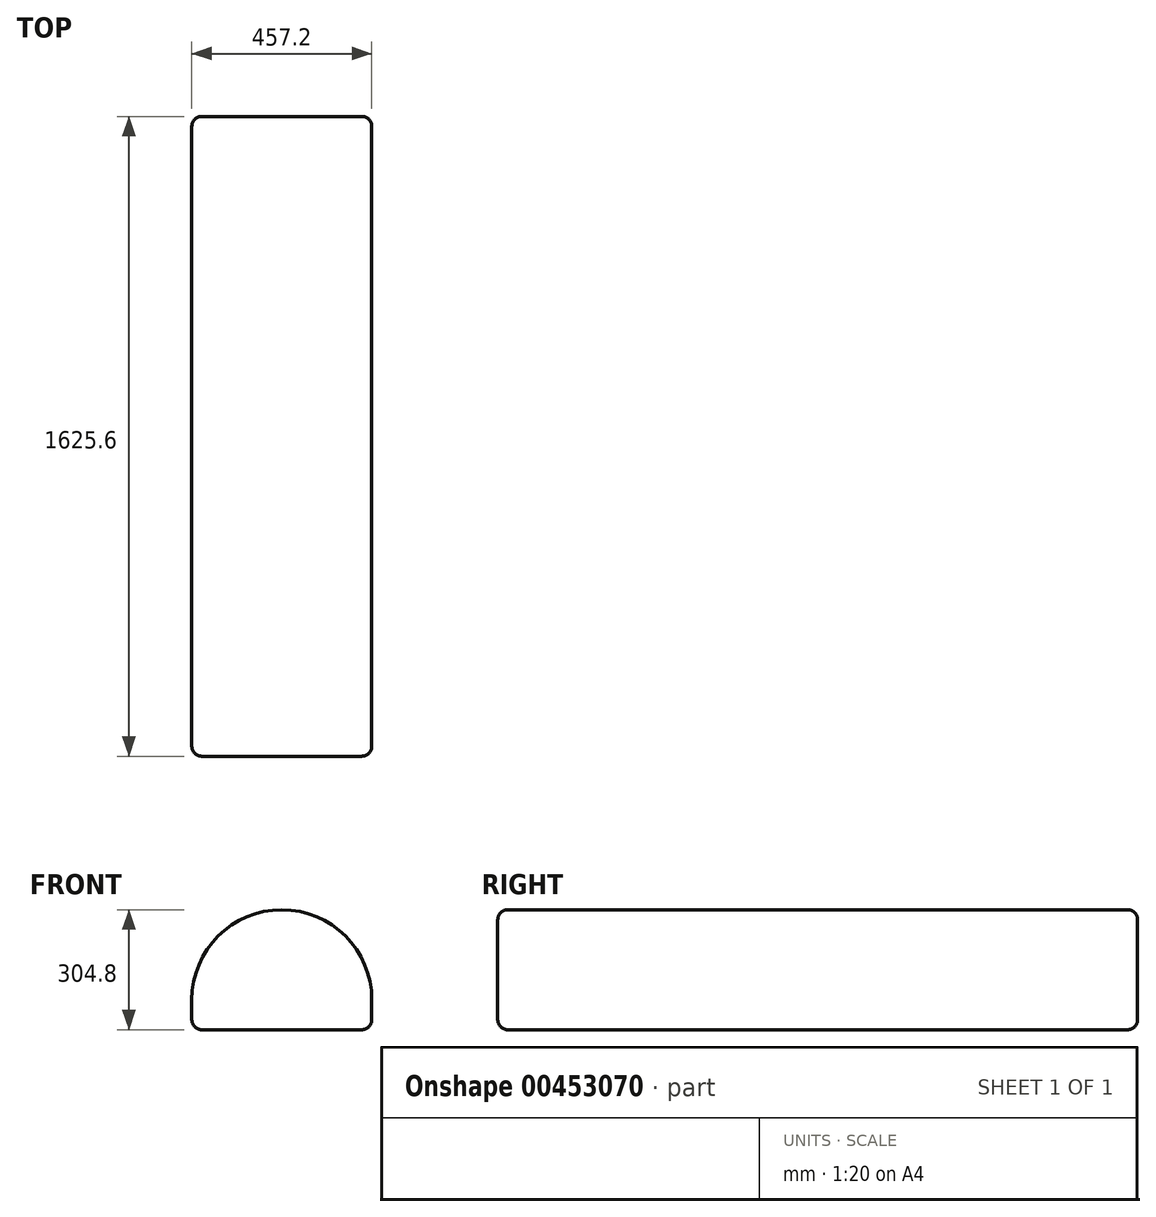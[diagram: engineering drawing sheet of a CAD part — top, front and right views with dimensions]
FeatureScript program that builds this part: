
annotation { "Feature Type Name" : "Feature", "Feature Type Description" : "" }
export const myFeature = defineFeature(function(context is Context, id is Id, definition is map)
    precondition{}
    {
        {
            var Q0;
            Q0=qCreatedBy(makeId("Front.planeOp"),FACE);
            var sketch = newSketch(context, id + "F0", { "sketchPlane" : qUnion([Q0])});
            skLineSegment(sketch, "E0", {"start": v(-228.6, 76.2) * mm, "end": v(-228.6, 0) * mm});
            skLineSegment(sketch, "E1", {"start": v(-228.6, 0) * mm, "end": v(228.6, 0) * mm});
            skLineSegment(sketch, "E2", {"start": v(228.6, 0) * mm, "end": v(228.6, 76.2) * mm});
            skArc(sketch, "E3", {"start": v(228.6, 76.2) * mm, "mid": v(0, 304.8) * mm, "end": v(-228.6, 76.2) * mm});
            skLineSegment(sketch, "E4", {"start": v(0, 304.8) * mm, "end": v(0, 0) * mm, "construction": true});
            skSolve(sketch);
        }
        {
            var Q0;
            Q0 = qSketchRegion(id + "F0", true);
            extrude(context, id + "F1", {"entities" : qUnion([Q0]), "depth" : 1625.6 * mm, "offsetDistance" : 25.4 * mm});
        }
        {
            var Q0;
            Q0=makeQuery(id+"F1.opExtrude","CAP_EDGE",EDGE,{"disambiguationData":[OSD([sQuery(id+"F0.wireOp",EDGE,"E3")])],"isStart":false});
            var Q1;
            Q1=makeQuery(id+"F1.opExtrude","CAP_EDGE",EDGE,{"disambiguationData":[OSD([sQuery(id+"F0.wireOp",EDGE,"E3")])],"isStart":true});
            var Q2;
            Q2=makeQuery(id+"F1.opExtrude","SWEPT_EDGE",EDGE,{"disambiguationData":[OSD([sQuery(id+"F0.wireOp",EDGE,"E1"),sQuery(id+"F0.wireOp",EDGE,"E2")])]});
            var Q3;
            Q3=makeQuery(id+"F1.opExtrude","CAP_EDGE",EDGE,{"disambiguationData":[OSD([sQuery(id+"F0.wireOp",EDGE,"E1")])],"isStart":false});
            var Q4;
            Q4=makeQuery(id+"F1.opExtrude","CAP_EDGE",EDGE,{"disambiguationData":[OSD([sQuery(id+"F0.wireOp",EDGE,"E1")])],"isStart":true});
            var Q5;
            Q5=makeQuery(id+"F1.opExtrude","SWEPT_EDGE",EDGE,{"disambiguationData":[OSD([sQuery(id+"F0.wireOp",EDGE,"E0"),sQuery(id+"F0.wireOp",EDGE,"E1")])]});
            fillet(context, id + "F2", {"entities" : qUnion([Q0, Q1, Q2, Q3, Q4, Q5]), "tangentPropagation" : true, "radius" : 25.4 * mm, "defaultsChanged" : false, "vertexSettings" : [], "allowEdgeOverflow" : false});
        }
    });
